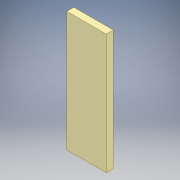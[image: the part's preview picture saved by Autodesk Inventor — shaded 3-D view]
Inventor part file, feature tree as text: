
AUTODESK INVENTOR PART (.ipt)
format: ipt  version: 2018 (Build 220112000, 112)  size: 93,696 bytes
history: native  units: mm
features: sketch x2, extrude x1
ambient origin geometry x8: Origin, YZ Plane, XZ Plane, XY Plane, X Axis, Y Axis, Z Axis, Center Point
bodies: 实体1 (feature_tree)
feature tree (3):
  extrude  "拉伸1"  Depth=17.0mm
  sketch  "草图2"  dims[d2=3.0mm d3=0.0mm]
  sketch  "草图1"  dims[d0=52.0mm d1=17.0mm]
